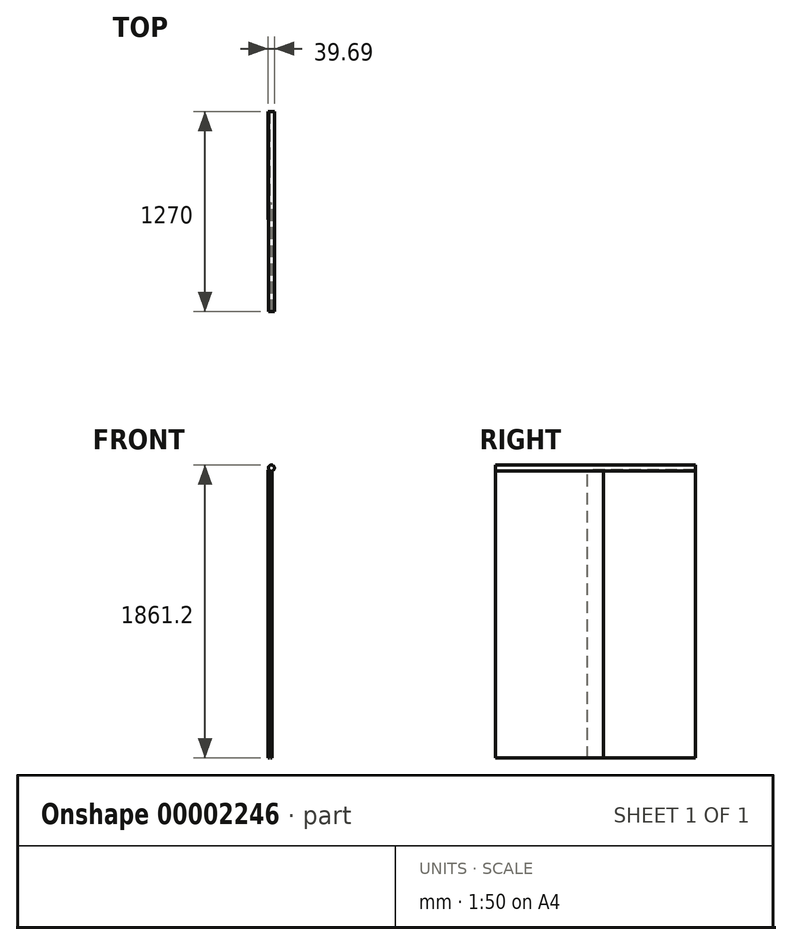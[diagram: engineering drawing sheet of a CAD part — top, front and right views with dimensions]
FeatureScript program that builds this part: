
annotation { "Feature Type Name" : "Feature", "Feature Type Description" : "" }
export const myFeature = defineFeature(function(context is Context, id is Id, definition is map)
    precondition{}
    {
        {
            var Q0;
            Q0=qCreatedBy(makeId("Right.planeOp"),FACE);
            var sketch = newSketch(context, id + "F0", { "sketchPlane" : qUnion([Q0])});
            skLineSegment(sketch, "E0.bottom", {"start": v(0, 0) * mm, "end": v(685.8, 0) * mm});
            skLineSegment(sketch, "E0.top", {"start": v(0, 1828.8) * mm, "end": v(685.8, 1828.8) * mm});
            skLineSegment(sketch, "E0.left", {"start": v(0, 0) * mm, "end": v(0, 1828.8) * mm});
            skLineSegment(sketch, "E0.right", {"start": v(685.8, 0) * mm, "end": v(685.8, 1828.8) * mm});
            skSolve(sketch);
        }
        {
            var Q0;
            Q0=makeQuery(id+"F0.imprint","IMPRINT",FACE,{"disambiguationData":[TD([[makeQuery(id+"F0.imprint","IMPRINT",EDGE,{"derivedFrom":sQuery(id+"F0.wireOp",EDGE,"E0.bottom")}),1.0]])]});
            extrude(context, id + "F1", {"entities" : qUnion([Q0]), "depth" : 9.52 * mm});
        }
        {
            var Q0;
            Q0=qCreatedBy(makeId("Right.planeOp"),FACE);
            cPlane(context, id + "F2", {"entities" : qUnion([Q0]), "cplaneType" : CPlaneType.OFFSET, "offset" : 6.35 * mm, "oppositeDirection" : true, "width" : 152.4 * mm, "height" : 152.4 * mm});
        }
        {
            var Q0;
            Q0=qCreatedBy(id+"F2.planeOp",FACE);
            var sketch = newSketch(context, id + "F3", { "sketchPlane" : qUnion([Q0])});
            skLineSegment(sketch, "E1.bottom", {"start": v(584.2, 0) * mm, "end": v(1270, 0) * mm});
            skLineSegment(sketch, "E1.top", {"start": v(584.2, 1828.8) * mm, "end": v(1270, 1828.8) * mm});
            skLineSegment(sketch, "E1.left", {"start": v(584.2, 0) * mm, "end": v(584.2, 1828.8) * mm});
            skLineSegment(sketch, "E1.right", {"start": v(1270, 0) * mm, "end": v(1270, 1828.8) * mm});
            skSolve(sketch);
        }
        {
            var Q0;
            Q0=makeQuery(id+"F3.imprint","IMPRINT",FACE,{"disambiguationData":[TD([[makeQuery(id+"F3.imprint","IMPRINT",EDGE,{"derivedFrom":sQuery(id+"F3.wireOp",EDGE,"E1.bottom")}),1.0]])]});
            extrude(context, id + "F4", {"entities" : qUnion([Q0]), "oppositeDirection" : true, "depth" : 9.52 * mm});
        }
        {
            var Q0;
            Q0=qCreatedBy(makeId("Front.planeOp"),FACE);
            var sketch = newSketch(context, id + "F5", { "sketchPlane" : qUnion([Q0])});
            skCircle(sketch, "E2", {"center": v(4.76, 1842.15) * mm, "radius": 19.05 * mm});
            skLineSegment(sketch, "E3", {"start": v(4.76, 1842.15) * mm, "end": v(4.76, 1828.8) * mm, "construction": true});
            skSolve(sketch);
        }
        {
            var Q0;
            Q0=makeQuery(id+"F5.imprint","IMPRINT",FACE,{"disambiguationData":[TD([[makeQuery(id+"F5.imprint","IMPRINT",EDGE,{"derivedFrom":sQuery(id+"F5.wireOp",EDGE,"E2")}),1.0]])]});
            extrude(context, id + "F6", {"entities" : qUnion([Q0]), "operationType" : NewBodyOperationType.ADD, "oppositeDirection" : true, "depth" : 1270 * mm});
        }
    });
